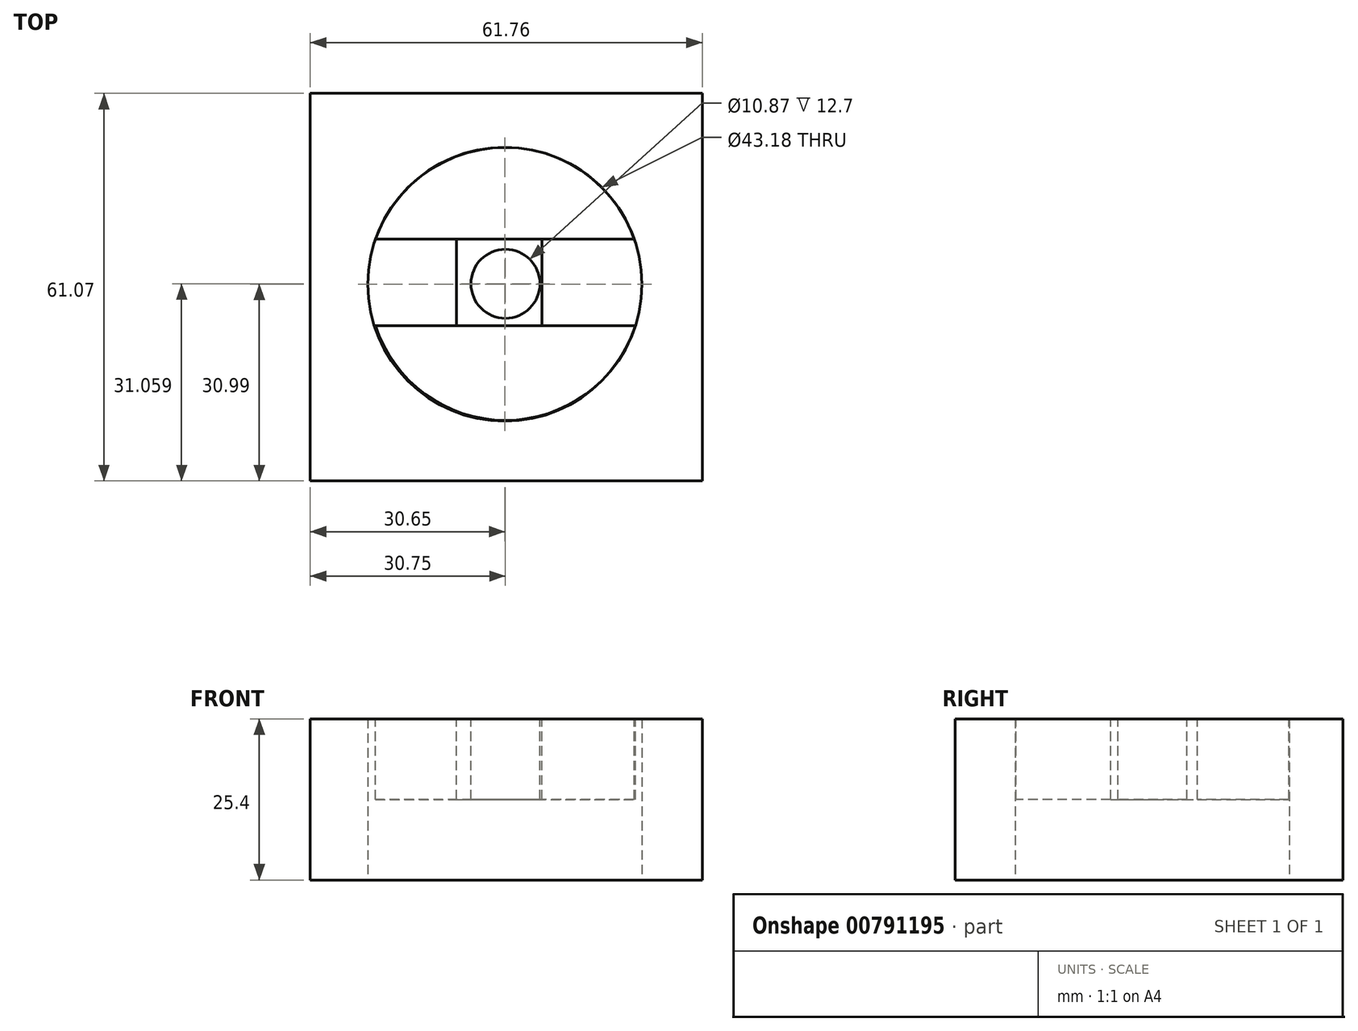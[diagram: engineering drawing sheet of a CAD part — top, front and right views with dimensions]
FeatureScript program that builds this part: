
annotation { "Feature Type Name" : "Feature", "Feature Type Description" : "" }
export const myFeature = defineFeature(function(context is Context, id is Id, definition is map)
    precondition{}
    {
        {
            var Q0;
            Q0=qCreatedBy(makeId("Top.planeOp"),FACE);
            var sketch = newSketch(context, id + "F0", { "sketchPlane" : qUnion([Q0])});
            skLineSegment(sketch, "E0.bottom", {"start": v(-30.65, 30.08) * mm, "end": v(31.1, 30.08) * mm});
            skLineSegment(sketch, "E0.top", {"start": v(-30.65, -31) * mm, "end": v(31.1, -31) * mm});
            skLineSegment(sketch, "E0.left", {"start": v(-30.65, 30.08) * mm, "end": v(-30.65, -31) * mm});
            skLineSegment(sketch, "E0.right", {"start": v(31.1, 30.08) * mm, "end": v(31.1, -31) * mm});
            skCircle(sketch, "E1", {"center": v(0, 0) * mm, "radius": 21.59 * mm});
            skSolve(sketch);
        }
        {
            var Q0;
            Q0=makeQuery(id+"F0.imprint","IMPRINT",FACE,{"disambiguationData":[TD([[makeQuery(id+"F0.imprint","IMPRINT",EDGE,{"derivedFrom":sQuery(id+"F0.wireOp",EDGE,"E0.bottom")}),-1.0]])]});
            extrude(context, id + "F1", {"entities" : qUnion([Q0]), "depth" : 25.4 * mm, "offsetDistance" : 25.4 * mm});
        }
        {
            var Q0;
            Q0=makeQuery(id+"F1.opExtrude","CAP_FACE",FACE,{"disambiguationData":[OSD([sQuery(id+"F0.wireOp",EDGE,"E0.bottom"),sQuery(id+"F0.wireOp",EDGE,"E0.top"),sQuery(id+"F0.wireOp",EDGE,"E0.left"),sQuery(id+"F0.wireOp",EDGE,"E0.right"),sQuery(id+"F0.wireOp",EDGE,"E1")])],"isStart":false});
            var sketch = newSketch(context, id + "F2", { "sketchPlane" : qUnion([Q0])});
            skLineSegment(sketch, "E2.bottom", {"start": v(-20.38, 7.12) * mm, "end": v(20.58, 7.12) * mm});
            skLineSegment(sketch, "E2.top", {"start": v(-20.38, -6.52) * mm, "end": v(20.58, -6.52) * mm});
            skLineSegment(sketch, "E2.left", {"start": v(-20.38, 7.12) * mm, "end": v(-20.38, -6.52) * mm});
            skLineSegment(sketch, "E2.right", {"start": v(20.58, 7.12) * mm, "end": v(20.58, -6.52) * mm});
            skArc(sketch, "E3", {"start": v(20.58, 7.12) * mm, "mid": v(0.1, 21.55) * mm, "end": v(-20.38, 7.12) * mm});
            skArc(sketch, "E4", {"start": v(-20.38, -6.52) * mm, "mid": v(0.1, -21.45) * mm, "end": v(20.58, -6.52) * mm});
            skLineSegment(sketch, "E5.bottom", {"start": v(-13.5, -6.52) * mm, "end": v(-7.64, -6.52) * mm});
            skLineSegment(sketch, "E5.top", {"start": v(-13.5, 7.12) * mm, "end": v(-7.64, 7.12) * mm});
            skLineSegment(sketch, "E5.left", {"start": v(-13.5, -6.52) * mm, "end": v(-13.5, 7.12) * mm});
            skLineSegment(sketch, "E5.right", {"start": v(-7.64, -6.52) * mm, "end": v(-7.64, 7.12) * mm});
            skLineSegment(sketch, "E6.bottom", {"start": v(5.82, -6.52) * mm, "end": v(12.7, -6.52) * mm});
            skLineSegment(sketch, "E6.top", {"start": v(5.82, 7.12) * mm, "end": v(12.7, 7.12) * mm});
            skLineSegment(sketch, "E6.left", {"start": v(5.82, -6.52) * mm, "end": v(5.82, 7.12) * mm});
            skLineSegment(sketch, "E6.right", {"start": v(12.7, -6.52) * mm, "end": v(12.7, 7.12) * mm});
            skCircle(sketch, "E7", {"center": v(0.1, 0.07) * mm, "radius": 5.43 * mm});
            skSolve(sketch);
        }
        {
            var Q0;
            {var subQ1=sQuery(id+"F2.wireOp",EDGE,"E2.bottom");var subQ2=makeQuery(id+"F1.opExtrude","CAP_EDGE",EDGE,{"disambiguationData":[OSD([sQuery(id+"F0.wireOp",EDGE,"E1")])],"isStart":false});var subQ4=makeQuery(id+"F2.imprint","INTERSECT",VERTEX,{"derivedFrom":[subQ2,subQ1]});Q0=makeQuery(id+"F2.imprint","IMPRINT",FACE,{"disambiguationData":[TD([[makeQuery(id+"F2.imprint","IMPRINT",EDGE,{"disambiguationData":[TD([[subQ4,-1.0]])],"derivedFrom":subQ2}),1.0]])]});}
            extrude(context, id + "F3", {"entities" : qUnion([Q0]), "oppositeDirection" : true, "depth" : 12.7 * mm, "offsetDistance" : 25.4 * mm});
        }
        {
            var Q0;
            Q0=makeQuery(id+"F2.imprint","IMPRINT",FACE,{"disambiguationData":[TD([[makeQuery(id+"F2.imprint","IMPRINT",EDGE,{"derivedFrom":sQuery(id+"F2.wireOp",EDGE,"E2.top")}),-1.0]])]});
            extrude(context, id + "F4", {"entities" : qUnion([Q0]), "oppositeDirection" : true, "depth" : 12.7 * mm, "offsetDistance" : 25.4 * mm});
        }
        {
            var Q0;
            {var subQ1=sQuery(id+"F2.wireOp",EDGE,"E5.right");Q0=makeQuery(id+"F2.imprint","IMPRINT",FACE,{"disambiguationData":[TD([[makeQuery(id+"F2.imprint","IMPRINT",EDGE,{"derivedFrom":subQ1}),-1.0]])]});}
            var Q1;
            Q1=makeQuery(id+"F2.imprint","IMPRINT",FACE,{"disambiguationData":[TD([[makeQuery(id+"F2.imprint","IMPRINT",EDGE,{"derivedFrom":sQuery(id+"F2.wireOp",EDGE,"E5.bottom")}),1.0]])]});
            var Q2;
            Q2=makeQuery(id+"F2.imprint","IMPRINT",FACE,{"disambiguationData":[TD([[makeQuery(id+"F2.imprint","IMPRINT",EDGE,{"derivedFrom":sQuery(id+"F2.wireOp",EDGE,"E6.bottom")}),1.0]])]});
            extrude(context, id + "F5", {"entities" : qUnion([Q0, Q1, Q2]), "oppositeDirection" : true, "depth" : 12.7 * mm, "offsetDistance" : 25.4 * mm});
        }
    });
